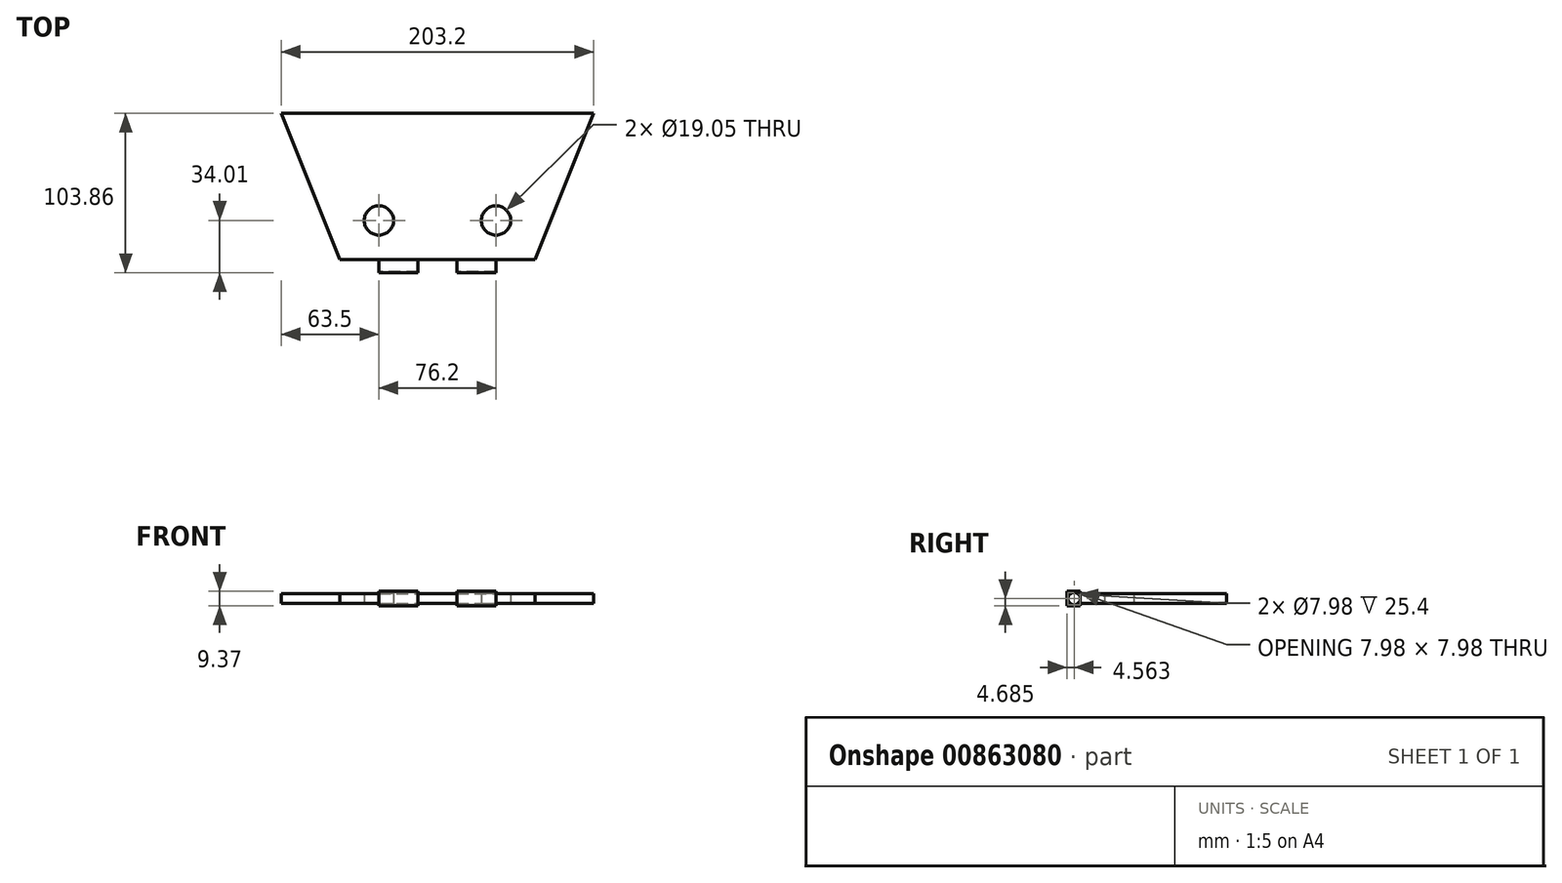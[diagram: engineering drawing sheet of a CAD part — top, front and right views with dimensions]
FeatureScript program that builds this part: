
annotation { "Feature Type Name" : "Feature", "Feature Type Description" : "" }
export const myFeature = defineFeature(function(context is Context, id is Id, definition is map)
    precondition{}
    {
        {
            var Q0;
            Q0=qCreatedBy(makeId("Top.planeOp"),FACE);
            var sketch = newSketch(context, id + "F0", { "sketchPlane" : qUnion([Q0])});
            skLineSegment(sketch, "E0", {"start": v(-63.5, 95.25) * mm, "end": v(-25.4, 0) * mm});
            skLineSegment(sketch, "E1", {"start": v(-25.4, 0) * mm, "end": v(101.6, 0) * mm});
            skLineSegment(sketch, "E2", {"start": v(101.6, 0) * mm, "end": v(139.7, 95.25) * mm});
            skLineSegment(sketch, "E3", {"start": v(139.7, 95.25) * mm, "end": v(-63.5, 95.25) * mm});
            skSolve(sketch);
        }
        {
            var Q0;
            Q0=makeQuery(id+"F0.imprint","IMPRINT",FACE,{"disambiguationData":[TD([[makeQuery(id+"F0.imprint","IMPRINT",EDGE,{"derivedFrom":sQuery(id+"F0.wireOp",EDGE,"E0")}),1.0]])]});
            extrude(context, id + "F1", {"entities" : qUnion([Q0]), "depth" : 6.35 * mm, "offsetDistance" : 25.4 * mm});
        }
        {
            var Q0;
            Q0=qCreatedBy(makeId("Right.planeOp"),FACE);
            var sketch = newSketch(context, id + "F2", { "sketchPlane" : qUnion([Q0])});
            skCircle(sketch, "E4", {"center": v(-4.05, 3.2) * mm, "radius": 3.99 * mm});
            skLineSegment(sketch, "E5.bottom", {"start": v(0, 7.89) * mm, "end": v(-8.61, 7.89) * mm});
            skLineSegment(sketch, "E5.top", {"start": v(0, -1.48) * mm, "end": v(-8.61, -1.48) * mm});
            skLineSegment(sketch, "E5.left", {"start": v(0, 7.89) * mm, "end": v(0, -1.48) * mm});
            skLineSegment(sketch, "E5.right", {"start": v(-8.61, 7.89) * mm, "end": v(-8.61, -1.48) * mm});
            skSolve(sketch);
        }
        {
            var Q0;
            Q0=qSketchRegion(id+"F2",true);
            var Q1;
            Q1=makeQuery(id+"F2.imprint","IMPRINT",FACE,{"disambiguationData":[TD([[makeQuery(id+"F2.imprint","IMPRINT",EDGE,{"derivedFrom":sQuery(id+"F2.wireOp",EDGE,"E4")}),-1.0]])]});
            extrude(context, id + "F3", {"entities" : qUnion([Q0, Q1]), "operationType" : NewBodyOperationType.ADD, "depth" : 76.2 * mm, "offsetDistance" : 25.4 * mm});
        }
        {
            var Q0;
            Q0=makeQuery(id+"F3.opExtrude","SWEPT_FACE",FACE,{"disambiguationData":[OSD([sQuery(id+"F2.wireOp",EDGE,"E5.bottom")])]});
            var sketch = newSketch(context, id + "F4", { "sketchPlane" : qUnion([Q0])});
            skLineSegment(sketch, "E6.bottom", {"start": v(50.8, 0) * mm, "end": v(25.4, 0) * mm});
            skLineSegment(sketch, "E6.top", {"start": v(50.8, -8.61) * mm, "end": v(25.4, -8.61) * mm});
            skLineSegment(sketch, "E6.left", {"start": v(50.8, 0) * mm, "end": v(50.8, -8.61) * mm});
            skLineSegment(sketch, "E6.right", {"start": v(25.4, 0) * mm, "end": v(25.4, -8.61) * mm});
            skSolve(sketch);
        }
        {
            var Q0;
            Q0=makeQuery(id+"F4.imprint","IMPRINT",FACE,{"disambiguationData":[TD([[makeQuery(id+"F4.imprint","IMPRINT",EDGE,{"derivedFrom":sQuery(id+"F4.wireOp",EDGE,"E6.bottom")}),1.0]])]});
            extrude(context, id + "F5", {"entities" : qUnion([Q0]), "operationType" : NewBodyOperationType.REMOVE, "oppositeDirection" : true, "depth" : 25.4 * mm, "offsetDistance" : 25.4 * mm});
        }
        {
            var Q0;
            Q0=makeQuery(id+"F1.opExtrude","CAP_FACE",FACE,{"disambiguationData":[OSD([sQuery(id+"F0.wireOp",EDGE,"E0"),sQuery(id+"F0.wireOp",EDGE,"E1"),sQuery(id+"F0.wireOp",EDGE,"E2"),sQuery(id+"F0.wireOp",EDGE,"E3")])],"isStart":true});
            var sketch = newSketch(context, id + "F6", { "sketchPlane" : qUnion([Q0])});
            skSolve(sketch);
        }
        {
            var Q0;
            {var subQ10=sQuery(id+"F0.wireOp",EDGE,"E0");Q0=makeQuery(id+"F6.imprint","IMPRINT",FACE,{"disambiguationData":[TD([[makeQuery(id+"F6.imprint","IMPRINT",EDGE,{"derivedFrom":makeQuery(id+"F1.opExtrude","CAP_EDGE",EDGE,{"disambiguationData":[OSD([subQ10])],"isStart":true})}),-1.0]])]});}
            var sketch = newSketch(context, id + "F7", { "sketchPlane" : qUnion([Q0])});
            skLineSegment(sketch, "E7", {"start": v(-35.9, -25.4) * mm, "end": v(111.76, -25.4) * mm});
            skCircle(sketch, "E8", {"center": v(0, -25.4) * mm, "radius": 9.53 * mm});
            skCircle(sketch, "E9", {"center": v(76.2, -25.4) * mm, "radius": 4.5 * mm});
            skSolve(sketch);
        }
        {
            var Q0;
            Q0=sQuery(id+"F7.wireOp",VERTEX,"E8.center");
            var Q1;
            Q1=sQuery(id+"F7.wireOp",VERTEX,"E9.center");
            var Q2;
            Q2=makeQuery(id+"F1.opExtrude","SWEPT_BODY",BODY,{"disambiguationData":[OSD([sQuery(id+"F0.wireOp",EDGE,"E0"),sQuery(id+"F0.wireOp",EDGE,"E1"),sQuery(id+"F0.wireOp",EDGE,"E2"),sQuery(id+"F0.wireOp",EDGE,"E3")])]});
            hole(context, id + "F8", {"style" : HoleStyle.SIMPLE, "endStyle" : HoleEndStyle.THROUGH, "holeDiameter" : 19.05 * mm, "majorDiameter" : 6.35 * mm, "isTappedThrough" : true, "tappedDepth" : 12.7 * mm, "tapClearance" : 3, "locations" : qUnion([Q0, Q1]), "scope" : qUnion([Q2])});
        }
    });
